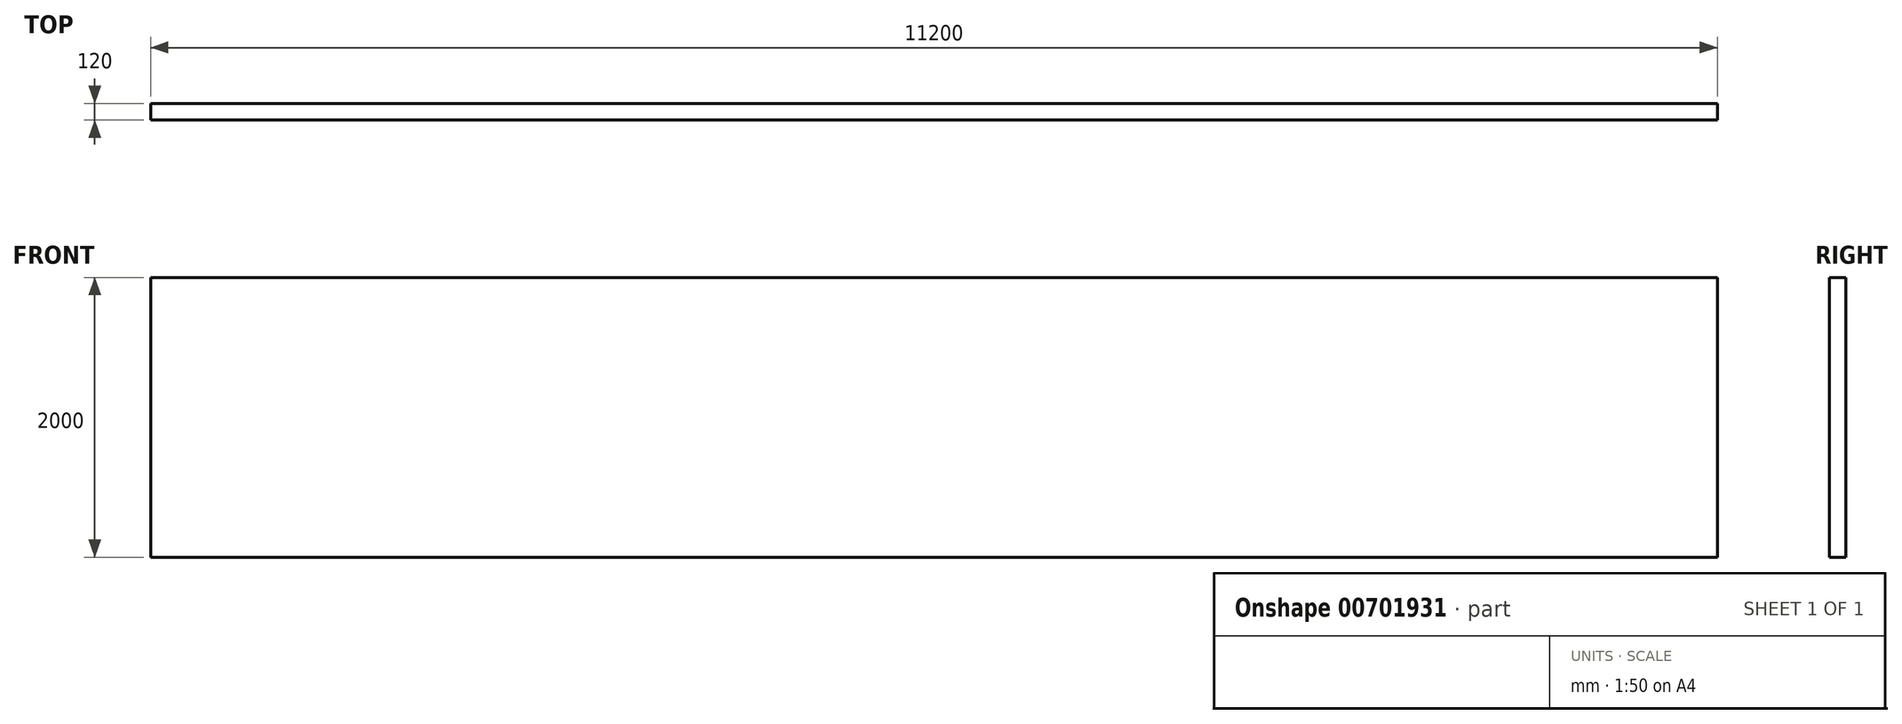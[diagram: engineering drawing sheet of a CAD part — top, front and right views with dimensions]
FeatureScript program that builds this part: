
annotation { "Feature Type Name" : "Feature", "Feature Type Description" : "" }
export const myFeature = defineFeature(function(context is Context, id is Id, definition is map)
    precondition{}
    {
        {
            var Q0;
            Q0=qCreatedBy(makeId("Top.planeOp"),FACE);
            var sketch = newSketch(context, id + "F0", { "sketchPlane" : qUnion([Q0])});
            skLineSegment(sketch, "E0.bottom", {"start": v(0, 0) * mm, "end": v(11200, 0) * mm});
            skLineSegment(sketch, "E0.top", {"start": v(0, 120) * mm, "end": v(11200, 120) * mm});
            skLineSegment(sketch, "E0.left", {"start": v(0, 0) * mm, "end": v(0, 120) * mm});
            skLineSegment(sketch, "E0.right", {"start": v(11200, 0) * mm, "end": v(11200, 120) * mm});
            skSolve(sketch);
        }
        {
            var Q0;
            Q0=makeQuery(id+"F0.imprint","IMPRINT",FACE,{"disambiguationData":[TD([[makeQuery(id+"F0.imprint","IMPRINT",EDGE,{"derivedFrom":sQuery(id+"F0.wireOp",EDGE,"E0.bottom")}),1.0]])]});
            extrude(context, id + "F1", {"entities" : qUnion([Q0]), "depth" : 2000 * mm, "offsetDistance" : 25 * mm});
        }
    });
